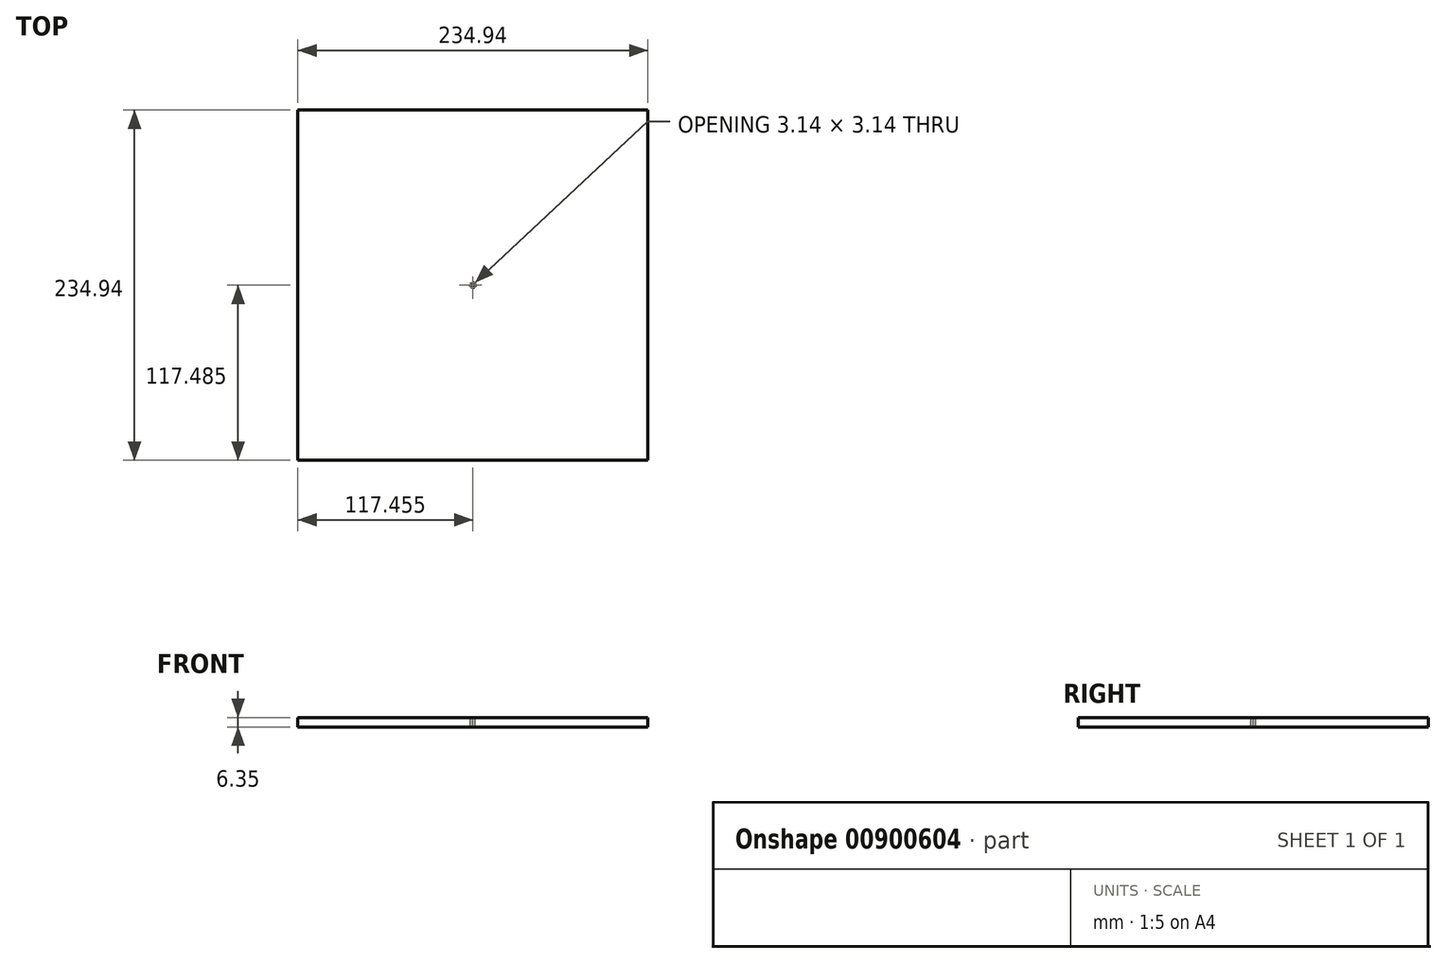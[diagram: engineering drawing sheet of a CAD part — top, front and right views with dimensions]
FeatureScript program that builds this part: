
annotation { "Feature Type Name" : "Feature", "Feature Type Description" : "" }
export const myFeature = defineFeature(function(context is Context, id is Id, definition is map)
    precondition{}
    {
        {
            var Q0;
            Q0=qCreatedBy(makeId("Top.planeOp"),FACE);
            var sketch = newSketch(context, id + "F0", { "sketchPlane" : qUnion([Q0])});
            skLineSegment(sketch, "E0.bottom", {"start": v(117.48, 117.48) * mm, "end": v(-117.48, 117.48) * mm});
            skLineSegment(sketch, "E0.top", {"start": v(117.47, -117.48) * mm, "end": v(-117.48, -117.48) * mm});
            skLineSegment(sketch, "E0.left", {"start": v(117.48, 117.48) * mm, "end": v(117.47, -117.48) * mm});
            skLineSegment(sketch, "E0.right", {"start": v(-117.48, 117.48) * mm, "end": v(-117.48, -117.48) * mm});
            skPoint(sketch, "E0.middle", {"position": v(0, 0) * mm});
            skSolve(sketch);
        }
        {
            var Q0;
            Q0=makeQuery(id+"F0.imprint","IMPRINT",FACE,{"disambiguationData":[TD([[makeQuery(id+"F0.imprint","IMPRINT",EDGE,{"derivedFrom":sQuery(id+"F0.wireOp",EDGE,"E0.bottom")}),1.0]])]});
            extrude(context, id + "F1", {"entities" : qUnion([Q0]), "depth" : 6.35 * mm, "offsetDistance" : 25.4 * mm});
        }
        {
            var Q0;
            Q0=makeQuery(id+"F1.opExtrude","CAP_FACE",FACE,{"disambiguationData":[OSD([sQuery(id+"F0.wireOp",EDGE,"E0.bottom"),sQuery(id+"F0.wireOp",EDGE,"E0.top"),sQuery(id+"F0.wireOp",EDGE,"E0.left"),sQuery(id+"F0.wireOp",EDGE,"E0.right")])],"isStart":false});
            var sketch = newSketch(context, id + "F2", { "sketchPlane" : qUnion([Q0])});
            skLineSegment(sketch, "E1.bottom", {"start": v(63.5, 63.5) * mm, "end": v(-63.5, 63.5) * mm});
            skLineSegment(sketch, "E1.top", {"start": v(63.5, -63.5) * mm, "end": v(-63.5, -63.5) * mm});
            skLineSegment(sketch, "E1.left", {"start": v(63.5, 63.5) * mm, "end": v(63.5, -63.5) * mm});
            skLineSegment(sketch, "E1.right", {"start": v(-63.5, 63.5) * mm, "end": v(-63.5, -63.5) * mm});
            skPoint(sketch, "E1.middle", {"position": v(0, 0) * mm});
            skLineSegment(sketch, "E2.bottom", {"start": v(-63.5, 63.5) * mm, "end": v(-88.9, 63.5) * mm});
            skLineSegment(sketch, "E2.top", {"start": v(-63.5, 88.9) * mm, "end": v(-88.9, 88.9) * mm});
            skLineSegment(sketch, "E2.left", {"start": v(-63.5, 63.5) * mm, "end": v(-63.5, 88.9) * mm});
            skLineSegment(sketch, "E2.right", {"start": v(-88.9, 63.5) * mm, "end": v(-88.9, 88.9) * mm});
            skLineSegment(sketch, "E3.bottom", {"start": v(63.5, 63.5) * mm, "end": v(88.9, 63.5) * mm});
            skLineSegment(sketch, "E3.top", {"start": v(63.5, 88.9) * mm, "end": v(88.9, 88.9) * mm});
            skLineSegment(sketch, "E3.left", {"start": v(63.5, 63.5) * mm, "end": v(63.5, 88.9) * mm});
            skLineSegment(sketch, "E3.right", {"start": v(88.9, 63.5) * mm, "end": v(88.9, 88.9) * mm});
            skLineSegment(sketch, "E4.bottom", {"start": v(63.5, -63.5) * mm, "end": v(88.9, -63.5) * mm});
            skLineSegment(sketch, "E4.top", {"start": v(63.5, -88.9) * mm, "end": v(88.9, -88.9) * mm});
            skLineSegment(sketch, "E4.left", {"start": v(63.5, -63.5) * mm, "end": v(63.5, -88.9) * mm});
            skLineSegment(sketch, "E4.right", {"start": v(88.9, -63.5) * mm, "end": v(88.9, -88.9) * mm});
            skLineSegment(sketch, "E5.bottom", {"start": v(-63.5, -63.5) * mm, "end": v(-88.9, -63.5) * mm});
            skLineSegment(sketch, "E5.top", {"start": v(-63.5, -88.9) * mm, "end": v(-88.9, -88.9) * mm});
            skLineSegment(sketch, "E5.left", {"start": v(-63.5, -63.5) * mm, "end": v(-63.5, -88.9) * mm});
            skLineSegment(sketch, "E5.right", {"start": v(-88.9, -63.5) * mm, "end": v(-88.9, -88.9) * mm});
            skLineSegment(sketch, "E6.bottom", {"start": v(-63.5, 63.5) * mm, "end": v(-38.1, 63.5) * mm});
            skLineSegment(sketch, "E6.top", {"start": v(-63.5, 38.1) * mm, "end": v(-38.1, 38.1) * mm});
            skLineSegment(sketch, "E6.left", {"start": v(-63.5, 63.5) * mm, "end": v(-63.5, 38.1) * mm});
            skLineSegment(sketch, "E6.right", {"start": v(-38.1, 63.5) * mm, "end": v(-38.1, 38.1) * mm});
            skLineSegment(sketch, "E7.bottom", {"start": v(63.5, 63.5) * mm, "end": v(38.1, 63.5) * mm});
            skLineSegment(sketch, "E7.top", {"start": v(63.5, 38.1) * mm, "end": v(38.1, 38.1) * mm});
            skLineSegment(sketch, "E7.left", {"start": v(63.5, 63.5) * mm, "end": v(63.5, 38.1) * mm});
            skLineSegment(sketch, "E7.right", {"start": v(38.1, 63.5) * mm, "end": v(38.1, 38.1) * mm});
            skLineSegment(sketch, "E8.bottom", {"start": v(63.5, -63.5) * mm, "end": v(38.1, -63.5) * mm});
            skLineSegment(sketch, "E8.top", {"start": v(63.5, -38.1) * mm, "end": v(38.1, -38.1) * mm});
            skLineSegment(sketch, "E8.left", {"start": v(63.5, -63.5) * mm, "end": v(63.5, -38.1) * mm});
            skLineSegment(sketch, "E8.right", {"start": v(38.1, -63.5) * mm, "end": v(38.1, -38.1) * mm});
            skLineSegment(sketch, "E9.bottom", {"start": v(-63.5, -63.5) * mm, "end": v(-38.1, -63.5) * mm});
            skLineSegment(sketch, "E9.top", {"start": v(-63.5, -38.1) * mm, "end": v(-38.1, -38.1) * mm});
            skLineSegment(sketch, "E9.left", {"start": v(-63.5, -63.5) * mm, "end": v(-63.5, -38.1) * mm});
            skLineSegment(sketch, "E9.right", {"start": v(-38.1, -63.5) * mm, "end": v(-38.1, -38.1) * mm});
            skLineSegment(sketch, "E10", {"start": v(-63.5, 0) * mm, "end": v(63.5, 0) * mm});
            skLineSegment(sketch, "E11", {"start": v(0, 63.5) * mm, "end": v(0, -63.5) * mm});
            skCircle(sketch, "E12", {"center": v(0, 0) * mm, "radius": 1.59 * mm});
            skSolve(sketch);
        }
        {
            var Q0;
            Q0=makeQuery(id+"F2.imprint","IMPRINT",FACE,{"disambiguationData":[TD([[makeQuery(id+"F2.imprint","IMPRINT",EDGE,{"derivedFrom":sQuery(id+"F2.wireOp",EDGE,"E6.bottom")}),-1.0]])]});
            var Q1;
            Q1=makeQuery(id+"F2.imprint","IMPRINT",FACE,{"disambiguationData":[TD([[makeQuery(id+"F2.imprint","IMPRINT",EDGE,{"derivedFrom":sQuery(id+"F2.wireOp",EDGE,"E7.bottom")}),1.0]])]});
            var Q2;
            Q2=makeQuery(id+"F2.imprint","IMPRINT",FACE,{"disambiguationData":[TD([[makeQuery(id+"F2.imprint","IMPRINT",EDGE,{"derivedFrom":sQuery(id+"F2.wireOp",EDGE,"E8.bottom")}),-1.0]])]});
            var Q3;
            Q3=makeQuery(id+"F2.imprint","IMPRINT",FACE,{"disambiguationData":[TD([[makeQuery(id+"F2.imprint","IMPRINT",EDGE,{"derivedFrom":sQuery(id+"F2.wireOp",EDGE,"E9.bottom")}),1.0]])]});
            var Q4;
            {var subQ0=sQuery(id+"F2.wireOp",EDGE,"E11");var subQ1=sQuery(id+"F2.wireOp",EDGE,"E10");var subQ2=makeQuery(id+"F2.imprint","INTERSECT",VERTEX,{"derivedFrom":[subQ1,subQ0]});Q4=makeQuery(id+"F2.imprint","IMPRINT",FACE,{"disambiguationData":[TD([[makeQuery(id+"F2.imprint","IMPRINT",EDGE,{"disambiguationData":[TD([[subQ2,-1.0]])],"derivedFrom":subQ1}),1.0]])]});}
            var Q5;
            {var subQ0=sQuery(id+"F2.wireOp",EDGE,"E12");var subQ1=sQuery(id+"F2.wireOp",EDGE,"E10");var subQ2=makeQuery(id+"F2.imprint","INTERSECT",VERTEX,{"disambiguationData":[OD(0.0)],"derivedFrom":[subQ1,subQ0]});Q5=makeQuery(id+"F2.imprint","IMPRINT",FACE,{"disambiguationData":[TD([[makeQuery(id+"F2.imprint","IMPRINT",EDGE,{"disambiguationData":[TD([[subQ2,-1.0]])],"derivedFrom":subQ1}),-1.0]])]});}
            var Q6;
            {var subQ0=sQuery(id+"F2.wireOp",EDGE,"E11");var subQ1=sQuery(id+"F2.wireOp",EDGE,"E10");var subQ2=makeQuery(id+"F2.imprint","INTERSECT",VERTEX,{"derivedFrom":[subQ1,subQ0]});Q6=makeQuery(id+"F2.imprint","IMPRINT",FACE,{"disambiguationData":[TD([[makeQuery(id+"F2.imprint","IMPRINT",EDGE,{"disambiguationData":[TD([[subQ2,-1.0]])],"derivedFrom":subQ1}),-1.0]])]});}
            extrude(context, id + "F3", {"entities" : qUnion([Q0, Q1, Q2, Q3, Q4, Q5, Q6]), "operationType" : NewBodyOperationType.REMOVE, "oppositeDirection" : true, "depth" : 25.4 * mm, "offsetDistance" : 25.4 * mm});
        }
    });
